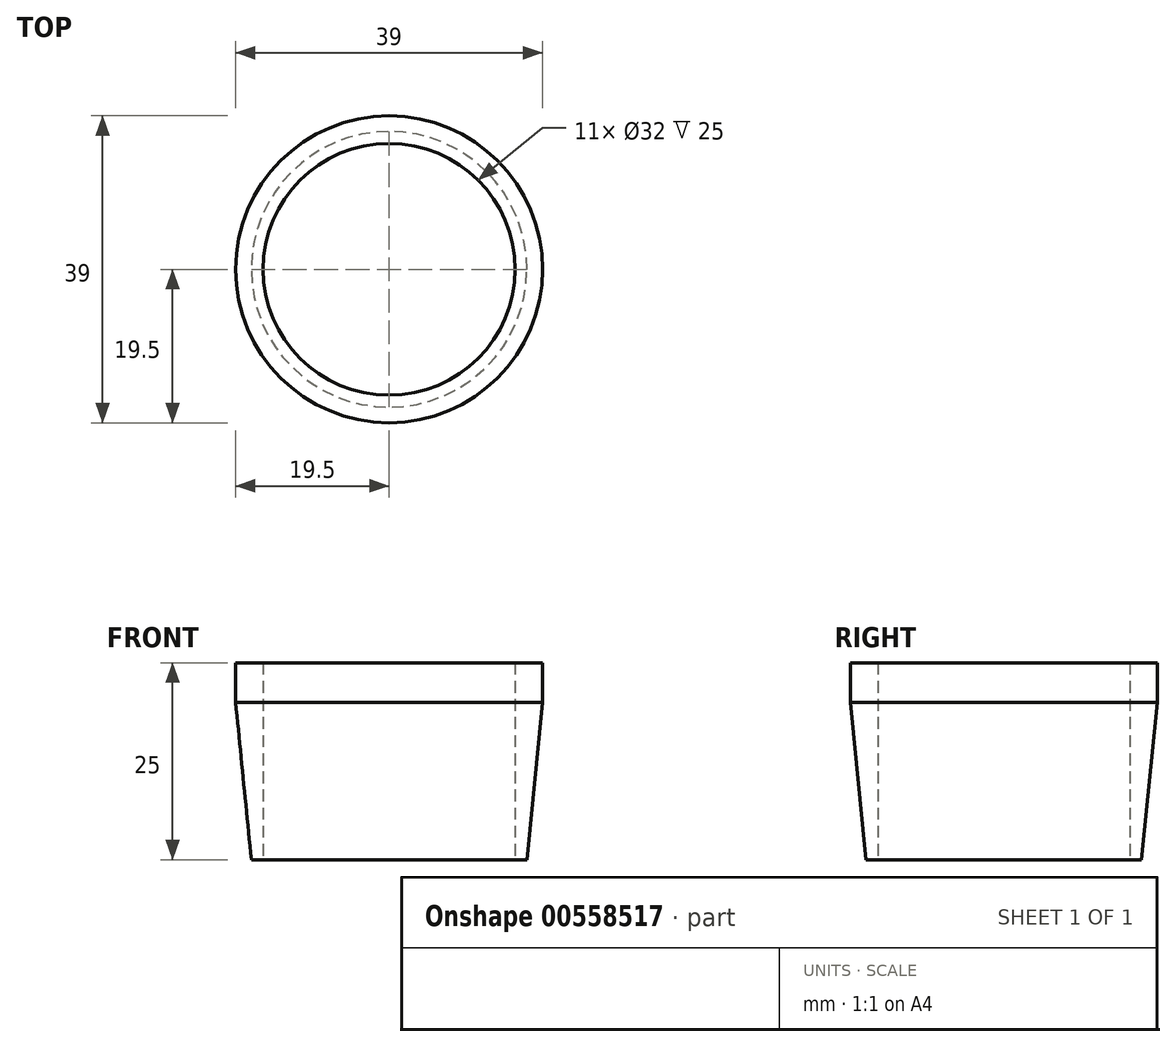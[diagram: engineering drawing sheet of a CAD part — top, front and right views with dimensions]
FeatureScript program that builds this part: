
annotation { "Feature Type Name" : "Feature", "Feature Type Description" : "" }
export const myFeature = defineFeature(function(context is Context, id is Id, definition is map)
    precondition{}
    {
        {
            var Q0;
            Q0=qCreatedBy(makeId("Front.planeOp"),FACE);
            var sketch = newSketch(context, id + "F0", { "sketchPlane" : qUnion([Q0])});
            skLineSegment(sketch, "E0", {"start": v(-16, 29.37) * mm, "end": v(-16, 4.37) * mm});
            skLineSegment(sketch, "E1", {"start": v(-16, 4.37) * mm, "end": v(-17.5, 4.37) * mm});
            skLineSegment(sketch, "E2", {"start": v(-17.5, 4.37) * mm, "end": v(-19.5, 24.37) * mm});
            skLineSegment(sketch, "E3", {"start": v(-19.5, 24.37) * mm, "end": v(-19.5, 29.37) * mm});
            skLineSegment(sketch, "E4", {"start": v(-19.5, 29.37) * mm, "end": v(-16, 29.37) * mm});
            skLineSegment(sketch, "E5", {"start": v(0, 0) * mm, "end": v(0, 33.7) * mm, "construction": true});
            skSolve(sketch);
        }
        {
            var Q0;
            Q0=makeQuery(id+"F0.imprint","IMPRINT",FACE,{"disambiguationData":[TD([[makeQuery(id+"F0.imprint","IMPRINT",EDGE,{"derivedFrom":sQuery(id+"F0.wireOp",EDGE,"E0")}),-1.0]])]});
            var Q1;
            Q1=sQuery(id+"F0.wireOp",EDGE,"E5");
            revolve(context, id + "F1", {"entities" : qUnion([Q0]), "axis" : qUnion([Q1]), "revolveType" : RevolveType.FULL});
        }
    });
